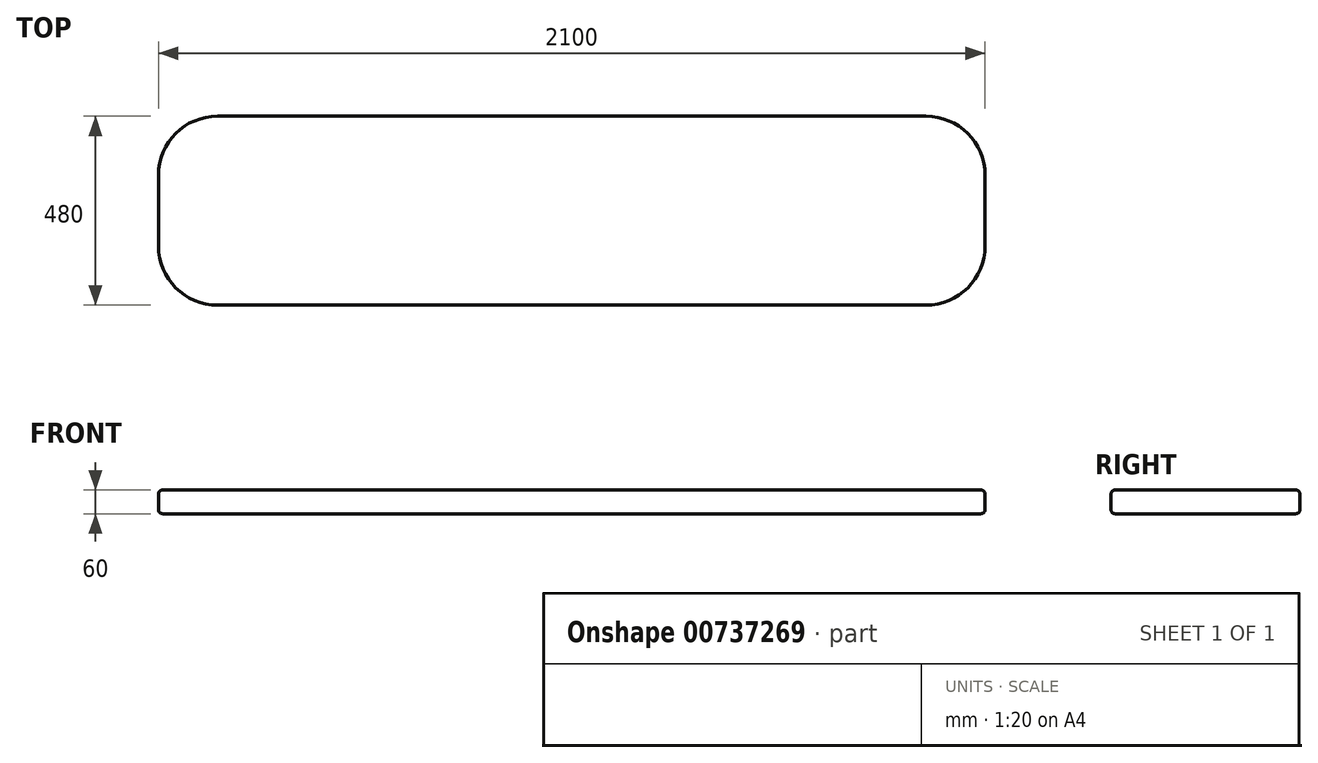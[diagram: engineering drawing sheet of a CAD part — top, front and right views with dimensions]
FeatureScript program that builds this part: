
annotation { "Feature Type Name" : "Feature", "Feature Type Description" : "" }
export const myFeature = defineFeature(function(context is Context, id is Id, definition is map)
    precondition{}
    {
        {
            var Q0;
            Q0=qCreatedBy(makeId("Top.planeOp"),FACE);
            var sketch = newSketch(context, id + "F0", { "sketchPlane" : qUnion([Q0])});
            skLineSegment(sketch, "E0.bottom", {"start": v(1050, 240) * mm, "end": v(-1050, 240) * mm});
            skLineSegment(sketch, "E0.top", {"start": v(1050, -240) * mm, "end": v(-1050, -240) * mm});
            skLineSegment(sketch, "E0.left", {"start": v(1050, 240) * mm, "end": v(1050, -240) * mm});
            skLineSegment(sketch, "E0.right", {"start": v(-1050, 240) * mm, "end": v(-1050, -240) * mm});
            skPoint(sketch, "E0.middle", {"position": v(0, 0) * mm});
            skSolve(sketch);
        }
        {
            var Q0;
            Q0=makeQuery(id+"F0.imprint","IMPRINT",FACE,{"disambiguationData":[TD([[makeQuery(id+"F0.imprint","IMPRINT",EDGE,{"derivedFrom":sQuery(id+"F0.wireOp",EDGE,"E0.bottom")}),1.0]])]});
            extrude(context, id + "F1", {"entities" : qUnion([Q0]), "depth" : 60 * mm, "offsetDistance" : 25 * mm});
        }
        {
            var Q0;
            Q0=makeQuery(id+"F1.opExtrude","SWEPT_EDGE",EDGE,{"disambiguationData":[OSD([sQuery(id+"F0.wireOp",EDGE,"E0.top"),sQuery(id+"F0.wireOp",EDGE,"E0.right")])]});
            var Q1;
            Q1=makeQuery(id+"F1.opExtrude","SWEPT_EDGE",EDGE,{"disambiguationData":[OSD([sQuery(id+"F0.wireOp",EDGE,"E0.bottom"),sQuery(id+"F0.wireOp",EDGE,"E0.right")])]});
            var Q2;
            Q2=makeQuery(id+"F1.opExtrude","SWEPT_EDGE",EDGE,{"disambiguationData":[OSD([sQuery(id+"F0.wireOp",EDGE,"E0.top"),sQuery(id+"F0.wireOp",EDGE,"E0.left")])]});
            var Q3;
            Q3=makeQuery(id+"F1.opExtrude","SWEPT_EDGE",EDGE,{"disambiguationData":[OSD([sQuery(id+"F0.wireOp",EDGE,"E0.bottom"),sQuery(id+"F0.wireOp",EDGE,"E0.left")])]});
            fillet(context, id + "F2", {"entities" : qUnion([Q0, Q1, Q2, Q3]), "radius" : 150 * mm, "tangentPropagation" : true, "allowEdgeOverflow" : false});
        }
        {
            var Q0;
            Q0=makeQuery(id+"F1.opExtrude","CAP_EDGE",EDGE,{"disambiguationData":[OSD([sQuery(id+"F0.wireOp",EDGE,"E0.top")])],"isStart":false});
            var Q1;
            Q1=makeQuery(id+"F1.opExtrude","CAP_EDGE",EDGE,{"disambiguationData":[OSD([sQuery(id+"F0.wireOp",EDGE,"E0.top")])],"isStart":true});
            fillet(context, id + "F3", {"entities" : qUnion([Q0, Q1]), "radius" : 10 * mm, "tangentPropagation" : true, "allowEdgeOverflow" : false});
        }
    });
